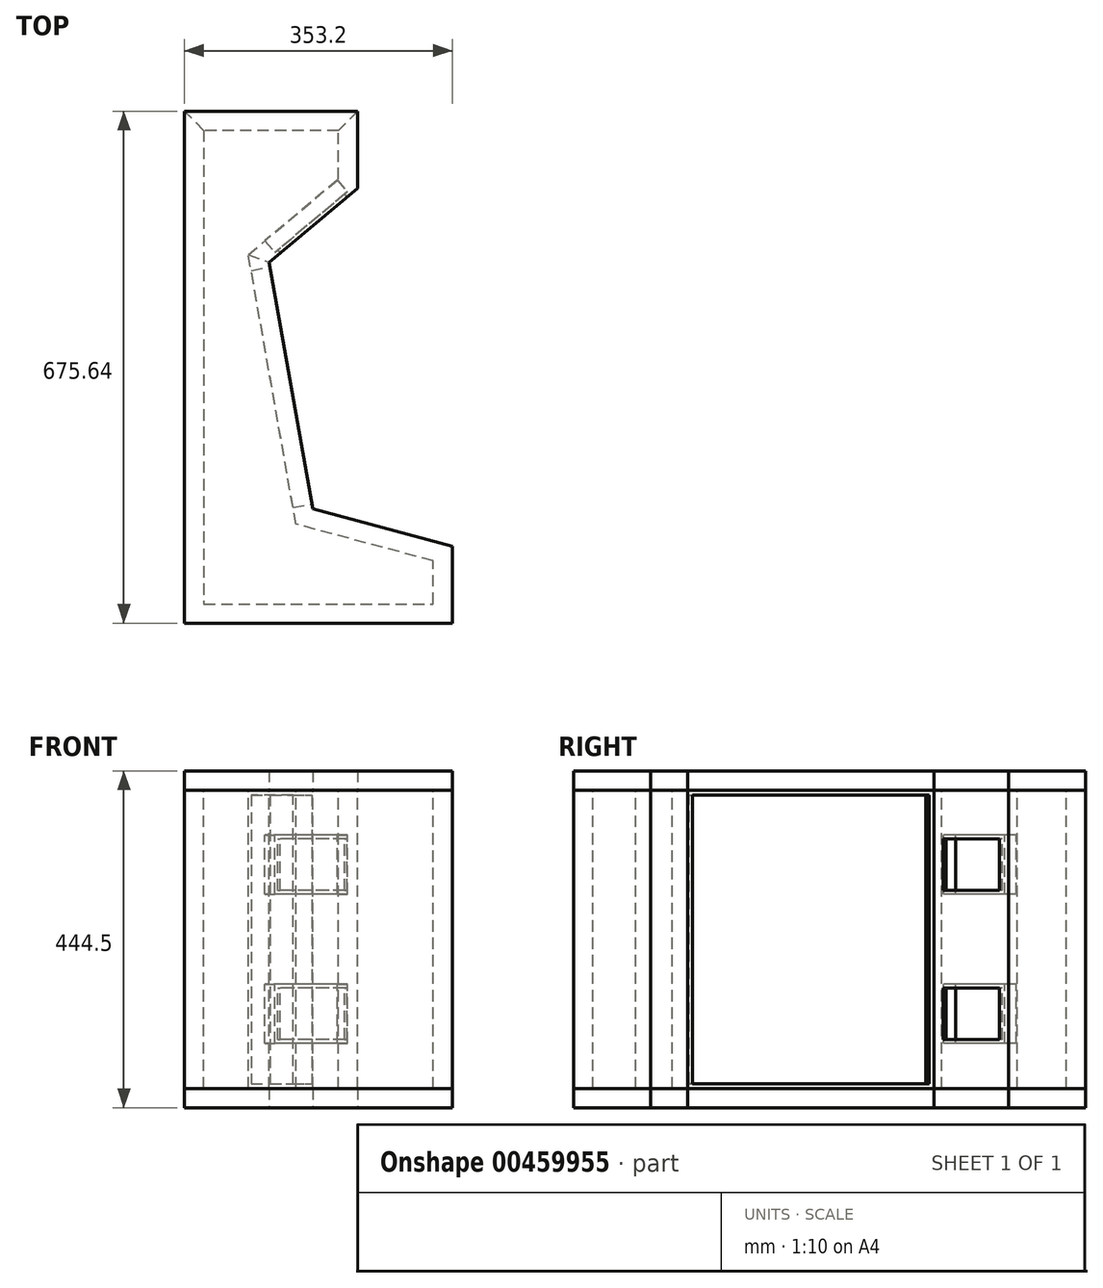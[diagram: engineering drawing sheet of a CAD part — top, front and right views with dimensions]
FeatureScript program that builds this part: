
annotation { "Feature Type Name" : "Feature", "Feature Type Description" : "" }
export const myFeature = defineFeature(function(context is Context, id is Id, definition is map)
    precondition{}
    {
        {
            var Q0;
            Q0=qCreatedBy(makeId("Top.planeOp"),FACE);
            var sketch = newSketch(context, id + "F0", { "sketchPlane" : qUnion([Q0])});
            skLineSegment(sketch, "E0", {"start": v(176.6, -337.82) * mm, "end": v(176.6, -236.22) * mm});
            skLineSegment(sketch, "E1", {"start": v(176.6, -236.22) * mm, "end": v(-7.4, -186.92) * mm});
            skLineSegment(sketch, "E2", {"start": v(-7.4, -186.92) * mm, "end": v(-64.75, 138.26) * mm});
            skLineSegment(sketch, "E3", {"start": v(-64.75, 138.26) * mm, "end": v(52, 236.22) * mm});
            skLineSegment(sketch, "E4", {"start": v(52, 236.22) * mm, "end": v(52, 337.82) * mm});
            skLineSegment(sketch, "E5", {"start": v(52, 337.82) * mm, "end": v(-176.6, 337.82) * mm});
            skLineSegment(sketch, "E6", {"start": v(-176.6, 337.82) * mm, "end": v(-176.6, -337.82) * mm});
            skLineSegment(sketch, "E7", {"start": v(-176.6, -337.82) * mm, "end": v(176.6, -337.82) * mm});
            skLineSegment(sketch, "E8", {"start": v(26.6, 248.07) * mm, "end": v(26.6, 312.42) * mm});
            skLineSegment(sketch, "E9", {"start": v(-92.3, 148.3) * mm, "end": v(26.6, 248.07) * mm});
            skLineSegment(sketch, "E10", {"start": v(26.6, 312.42) * mm, "end": v(-151.2, 312.42) * mm});
            skLineSegment(sketch, "E11", {"start": v(-29.61, -207.27) * mm, "end": v(-92.3, 148.3) * mm});
            skLineSegment(sketch, "E12", {"start": v(-151.2, 312.42) * mm, "end": v(-151.2, -312.42) * mm});
            skLineSegment(sketch, "E13", {"start": v(-151.2, -312.42) * mm, "end": v(151.2, -312.42) * mm});
            skLineSegment(sketch, "E14", {"start": v(151.2, -312.42) * mm, "end": v(151.2, -255.71) * mm});
            skLineSegment(sketch, "E15", {"start": v(151.2, -255.71) * mm, "end": v(-29.61, -207.27) * mm});
            skLineSegment(sketch, "E16", {"start": v(-151.2, 312.42) * mm, "end": v(-176.6, 337.82) * mm});
            skLineSegment(sketch, "E17", {"start": v(52, 337.82) * mm, "end": v(26.6, 312.42) * mm});
            skLineSegment(sketch, "E18", {"start": v(26.6, 248.07) * mm, "end": v(52, 236.22) * mm});
            skLineSegment(sketch, "E19", {"start": v(-92.3, 148.3) * mm, "end": v(-64.75, 138.26) * mm});
            skLineSegment(sketch, "E20", {"start": v(-7.4, -186.92) * mm, "end": v(-29.61, -207.27) * mm});
            skLineSegment(sketch, "E21", {"start": v(176.6, -236.22) * mm, "end": v(151.2, -255.71) * mm});
            skLineSegment(sketch, "E22", {"start": v(151.2, -312.42) * mm, "end": v(176.6, -337.82) * mm});
            skLineSegment(sketch, "E23", {"start": v(-151.2, -312.42) * mm, "end": v(-176.6, -337.82) * mm});
            skSolve(sketch);
        }
        {
            var Q0;
            Q0=makeQuery(id+"F0.imprint","IMPRINT",FACE,{"disambiguationData":[TD([[makeQuery(id+"F0.imprint","IMPRINT",EDGE,{"derivedFrom":sQuery(id+"F0.wireOp",EDGE,"E3")}),1.0]])]});
            extrude(context, id + "F1", {"entities" : qUnion([Q0]), "oppositeDirection" : true, "depth" : 393.7 * mm});
        }
        {
            var Q0;
            Q0=makeQuery(id+"F1.opExtrude","SWEPT_FACE",FACE,{"disambiguationData":[OSD([sQuery(id+"F0.wireOp",EDGE,"E3")])]});
            var sketch = newSketch(context, id + "F2", { "sketchPlane" : qUnion([Q0])});
            skPoint(sketch, "E24", {"position": v(115.48, -196.85) * mm});
            skPoint(sketch, "E24.positionSnap0", {"position": v(115.48, 0) * mm});
            skPoint(sketch, "E24.positionSnap1", {"position": v(191.68, -196.85) * mm});
            skLineSegment(sketch, "E25", {"start": v(191.68, 0) * mm, "end": v(191.68, -196.85) * mm});
            skLineSegment(sketch, "E26", {"start": v(191.68, -196.85) * mm, "end": v(191.68, -393.7) * mm});
            skPoint(sketch, "E27", {"position": v(115.48, -98.43) * mm});
            skPoint(sketch, "E27.positionSnap0", {"position": v(191.68, -98.43) * mm});
            skPoint(sketch, "E28", {"position": v(115.48, -295.28) * mm});
            skPoint(sketch, "E28.positionSnap0", {"position": v(191.68, -295.28) * mm});
            skLineSegment(sketch, "E29.bottom", {"start": v(177.96, -137.41) * mm, "end": v(53, -137.41) * mm});
            skLineSegment(sketch, "E29.top", {"start": v(177.96, -59.44) * mm, "end": v(53, -59.44) * mm});
            skLineSegment(sketch, "E29.left", {"start": v(177.96, -137.41) * mm, "end": v(177.96, -59.44) * mm});
            skLineSegment(sketch, "E29.right", {"start": v(53, -137.41) * mm, "end": v(53, -59.44) * mm});
            skLineSegment(sketch, "E30.bottom", {"start": v(177.96, -334.26) * mm, "end": v(53, -334.26) * mm});
            skLineSegment(sketch, "E30.top", {"start": v(177.96, -256.29) * mm, "end": v(53, -256.29) * mm});
            skLineSegment(sketch, "E30.left", {"start": v(177.96, -334.26) * mm, "end": v(177.96, -256.29) * mm});
            skLineSegment(sketch, "E30.right", {"start": v(53, -334.26) * mm, "end": v(53, -256.29) * mm});
            skLineSegment(sketch, "E31.0", {"start": v(172.88, -329.18) * mm, "end": v(172.88, -261.37) * mm});
            skLineSegment(sketch, "E31.1", {"start": v(172.88, -329.18) * mm, "end": v(58.07, -329.18) * mm});
            skLineSegment(sketch, "E31.2", {"start": v(58.07, -329.18) * mm, "end": v(58.07, -261.37) * mm});
            skLineSegment(sketch, "E31.3", {"start": v(172.88, -261.37) * mm, "end": v(58.07, -261.37) * mm});
            skLineSegment(sketch, "E32.0", {"start": v(172.88, -132.33) * mm, "end": v(172.88, -64.52) * mm});
            skLineSegment(sketch, "E32.1", {"start": v(172.88, -132.33) * mm, "end": v(58.07, -132.33) * mm});
            skLineSegment(sketch, "E32.2", {"start": v(58.07, -132.33) * mm, "end": v(58.07, -64.52) * mm});
            skLineSegment(sketch, "E32.3", {"start": v(172.88, -64.52) * mm, "end": v(58.07, -64.52) * mm});
            skLineSegment(sketch, "E33", {"start": v(135.35, -256.29) * mm, "end": v(135.35, -137.41) * mm});
            skSolve(sketch);
        }
        {
            var Q0;
            Q0=makeQuery(id+"F0.imprint","IMPRINT",FACE,{"disambiguationData":[TD([[makeQuery(id+"F0.imprint","IMPRINT",EDGE,{"derivedFrom":sQuery(id+"F0.wireOp",EDGE,"E2")}),1.0]])]});
            extrude(context, id + "F3", {"entities" : qUnion([Q0]), "oppositeDirection" : true, "depth" : 393.7 * mm});
        }
        {
            var Q0;
            Q0=makeQuery(id+"F0.imprint","IMPRINT",FACE,{"disambiguationData":[TD([[makeQuery(id+"F0.imprint","IMPRINT",EDGE,{"derivedFrom":sQuery(id+"F0.wireOp",EDGE,"E1")}),1.0]])]});
            extrude(context, id + "F4", {"entities" : qUnion([Q0]), "operationType" : NewBodyOperationType.ADD, "oppositeDirection" : true, "depth" : 393.7 * mm});
        }
        {
            var Q0;
            Q0=makeQuery(id+"F0.imprint","IMPRINT",FACE,{"disambiguationData":[TD([[makeQuery(id+"F0.imprint","IMPRINT",EDGE,{"derivedFrom":sQuery(id+"F0.wireOp",EDGE,"E0")}),1.0]])]});
            extrude(context, id + "F5", {"entities" : qUnion([Q0]), "operationType" : NewBodyOperationType.ADD, "oppositeDirection" : true, "depth" : 393.7 * mm});
        }
        {
            var Q0;
            Q0=makeQuery(id+"F0.imprint","IMPRINT",FACE,{"disambiguationData":[TD([[makeQuery(id+"F0.imprint","IMPRINT",EDGE,{"derivedFrom":sQuery(id+"F0.wireOp",EDGE,"E7")}),1.0]])]});
            extrude(context, id + "F6", {"entities" : qUnion([Q0]), "operationType" : NewBodyOperationType.ADD, "oppositeDirection" : true, "depth" : 393.7 * mm});
        }
        {
            var Q0;
            Q0=makeQuery(id+"F0.imprint","IMPRINT",FACE,{"disambiguationData":[TD([[makeQuery(id+"F0.imprint","IMPRINT",EDGE,{"derivedFrom":sQuery(id+"F0.wireOp",EDGE,"E4")}),1.0]])]});
            extrude(context, id + "F7", {"entities" : qUnion([Q0]), "operationType" : NewBodyOperationType.ADD, "oppositeDirection" : true, "depth" : 393.7 * mm});
        }
        {
            var Q0;
            Q0=makeQuery(id+"F0.imprint","IMPRINT",FACE,{"disambiguationData":[TD([[makeQuery(id+"F0.imprint","IMPRINT",EDGE,{"derivedFrom":sQuery(id+"F0.wireOp",EDGE,"E6")}),1.0]])]});
            extrude(context, id + "F8", {"entities" : qUnion([Q0]), "operationType" : NewBodyOperationType.ADD, "oppositeDirection" : true, "depth" : 393.7 * mm});
        }
        {
            var Q0;
            Q0=makeQuery(id+"F0.imprint","IMPRINT",FACE,{"disambiguationData":[TD([[makeQuery(id+"F0.imprint","IMPRINT",EDGE,{"derivedFrom":sQuery(id+"F0.wireOp",EDGE,"E5")}),1.0]])]});
            extrude(context, id + "F9", {"entities" : qUnion([Q0]), "oppositeDirection" : true, "depth" : 393.7 * mm});
        }
        {
            var Q0;
            Q0=makeQuery(id+"F0.imprint","IMPRINT",FACE,{"disambiguationData":[TD([[makeQuery(id+"F0.imprint","IMPRINT",EDGE,{"derivedFrom":sQuery(id+"F0.wireOp",EDGE,"E8")}),1.0]])]});
            var Q1;
            Q1=makeQuery(id+"F0.imprint","IMPRINT",FACE,{"disambiguationData":[TD([[makeQuery(id+"F0.imprint","IMPRINT",EDGE,{"derivedFrom":sQuery(id+"F0.wireOp",EDGE,"E3")}),1.0]])]});
            var Q2;
            Q2=makeQuery(id+"F0.imprint","IMPRINT",FACE,{"disambiguationData":[TD([[makeQuery(id+"F0.imprint","IMPRINT",EDGE,{"derivedFrom":sQuery(id+"F0.wireOp",EDGE,"E5")}),1.0]])]});
            var Q3;
            Q3=makeQuery(id+"F0.imprint","IMPRINT",FACE,{"disambiguationData":[TD([[makeQuery(id+"F0.imprint","IMPRINT",EDGE,{"derivedFrom":sQuery(id+"F0.wireOp",EDGE,"E6")}),1.0]])]});
            var Q4;
            Q4=makeQuery(id+"F0.imprint","IMPRINT",FACE,{"disambiguationData":[TD([[makeQuery(id+"F0.imprint","IMPRINT",EDGE,{"derivedFrom":sQuery(id+"F0.wireOp",EDGE,"E4")}),1.0]])]});
            var Q5;
            Q5=makeQuery(id+"F0.imprint","IMPRINT",FACE,{"disambiguationData":[TD([[makeQuery(id+"F0.imprint","IMPRINT",EDGE,{"derivedFrom":sQuery(id+"F0.wireOp",EDGE,"E7")}),1.0]])]});
            var Q6;
            Q6=makeQuery(id+"F0.imprint","IMPRINT",FACE,{"disambiguationData":[TD([[makeQuery(id+"F0.imprint","IMPRINT",EDGE,{"derivedFrom":sQuery(id+"F0.wireOp",EDGE,"E0")}),1.0]])]});
            var Q7;
            Q7=makeQuery(id+"F0.imprint","IMPRINT",FACE,{"disambiguationData":[TD([[makeQuery(id+"F0.imprint","IMPRINT",EDGE,{"derivedFrom":sQuery(id+"F0.wireOp",EDGE,"E1")}),1.0]])]});
            var Q8;
            Q8=makeQuery(id+"F0.imprint","IMPRINT",FACE,{"disambiguationData":[TD([[makeQuery(id+"F0.imprint","IMPRINT",EDGE,{"derivedFrom":sQuery(id+"F0.wireOp",EDGE,"E2")}),1.0]])]});
            extrude(context, id + "F10", {"entities" : qUnion([Q0, Q1, Q2, Q3, Q4, Q5, Q6, Q7, Q8]), "depth" : 25.4 * mm});
        }
        {
            var Q0;
            Q0=makeQuery(id+"F10.opExtrude","SWEPT_BODY",BODY,{"disambiguationData":[OSD([sQuery(id+"F0.wireOp",EDGE,"E0"),sQuery(id+"F0.wireOp",EDGE,"E1"),sQuery(id+"F0.wireOp",EDGE,"E2"),sQuery(id+"F0.wireOp",EDGE,"E3"),sQuery(id+"F0.wireOp",EDGE,"E4"),sQuery(id+"F0.wireOp",EDGE,"E5"),sQuery(id+"F0.wireOp",EDGE,"E6"),sQuery(id+"F0.wireOp",EDGE,"E7")])]});
            transform(context, id + "F11", {"entities" : qUnion([Q0]), "transformType" : TransformType.TRANSLATION_3D, "dx" : 0 * mm, "dy" : 0 * mm, "dz" : -419.1 * mm, "makeCopy" : true});
        }
        {
            var Q0;
            Q0=makeQuery(id+"F2.imprint","IMPRINT",FACE,{"disambiguationData":[TD([[makeQuery(id+"F2.imprint","IMPRINT",EDGE,{"derivedFrom":sQuery(id+"F2.wireOp",EDGE,"E32.0")}),1.0]])]});
            var Q1;
            Q1=makeQuery(id+"F2.imprint","IMPRINT",FACE,{"disambiguationData":[TD([[makeQuery(id+"F2.imprint","IMPRINT",EDGE,{"derivedFrom":sQuery(id+"F2.wireOp",EDGE,"E31.0")}),1.0]])]});
            extrude(context, id + "F12", {"entities" : qUnion([Q0, Q1]), "operationType" : NewBodyOperationType.REMOVE, "oppositeDirection" : true, "depth" : 25.4 * mm});
        }
        {
            var Q0;
            Q0=makeQuery(id+"F2.imprint","IMPRINT",FACE,{"disambiguationData":[TD([[makeQuery(id+"F2.imprint","IMPRINT",EDGE,{"derivedFrom":sQuery(id+"F2.wireOp",EDGE,"E29.bottom")}),-1.0]])]});
            var Q1;
            Q1=makeQuery(id+"F2.imprint","IMPRINT",FACE,{"disambiguationData":[TD([[makeQuery(id+"F2.imprint","IMPRINT",EDGE,{"derivedFrom":sQuery(id+"F2.wireOp",EDGE,"E30.bottom")}),-1.0]])]});
            extrude(context, id + "F13", {"entities" : qUnion([Q0, Q1]), "operationType" : NewBodyOperationType.REMOVE, "oppositeDirection" : true, "depth" : 25.4 * mm});
        }
        {
            var Q0;
            Q0=makeQuery(id+"F2.imprint","IMPRINT",FACE,{"disambiguationData":[TD([[makeQuery(id+"F2.imprint","IMPRINT",EDGE,{"derivedFrom":sQuery(id+"F2.wireOp",EDGE,"E29.bottom")}),-1.0]])]});
            var Q1;
            Q1=makeQuery(id+"F2.imprint","IMPRINT",FACE,{"disambiguationData":[TD([[makeQuery(id+"F2.imprint","IMPRINT",EDGE,{"derivedFrom":sQuery(id+"F2.wireOp",EDGE,"E30.bottom")}),-1.0]])]});
            extrude(context, id + "F14", {"entities" : qUnion([Q0, Q1]), "operationType" : NewBodyOperationType.ADD, "oppositeDirection" : true, "depth" : 5.08 * mm});
        }
        {
            var Q0;
            Q0=makeQuery(id+"F3.opExtrude","SWEPT_FACE",FACE,{"disambiguationData":[OSD([sQuery(id+"F0.wireOp",EDGE,"E2")])]});
            var sketch = newSketch(context, id + "F15", { "sketchPlane" : qUnion([Q0])});
            skLineSegment(sketch, "E34.bottom", {"start": v(147.4, 0) * mm, "end": v(-182.8, 0) * mm});
            skLineSegment(sketch, "E34.top", {"start": v(147.4, -393.7) * mm, "end": v(-182.8, -393.7) * mm});
            skLineSegment(sketch, "E34.left", {"start": v(147.4, 0) * mm, "end": v(147.4, -393.7) * mm});
            skLineSegment(sketch, "E34.right", {"start": v(-182.8, 0) * mm, "end": v(-182.8, -393.7) * mm});
            skLineSegment(sketch, "E35.0", {"start": v(141.06, -6.35) * mm, "end": v(141.06, -387.35) * mm});
            skLineSegment(sketch, "E35.1", {"start": v(141.06, -6.35) * mm, "end": v(-176.44, -6.35) * mm});
            skLineSegment(sketch, "E35.2", {"start": v(-176.44, -6.35) * mm, "end": v(-176.44, -387.35) * mm});
            skLineSegment(sketch, "E35.3", {"start": v(141.06, -387.35) * mm, "end": v(-176.44, -387.35) * mm});
            skSolve(sketch);
        }
        {
            var Q0;
            Q0=makeQuery(id+"F15.imprint","IMPRINT",FACE,{"disambiguationData":[TD([[makeQuery(id+"F15.imprint","IMPRINT",EDGE,{"derivedFrom":sQuery(id+"F15.wireOp",EDGE,"E35.0")}),-1.0]])]});
            extrude(context, id + "F16", {"entities" : qUnion([Q0]), "operationType" : NewBodyOperationType.REMOVE, "oppositeDirection" : true, "depth" : 25.4 * mm});
        }
    });
